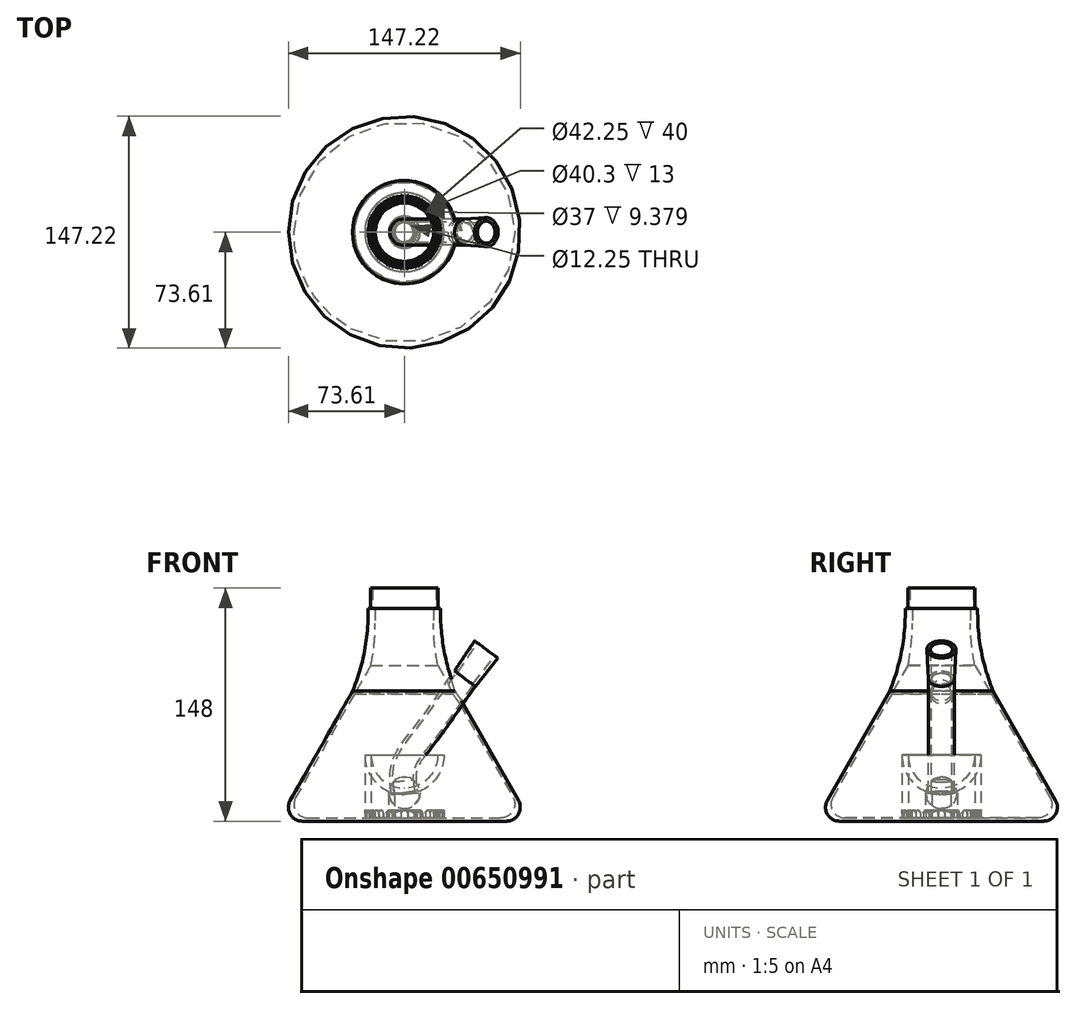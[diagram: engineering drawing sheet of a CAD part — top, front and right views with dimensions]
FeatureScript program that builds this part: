
annotation { "Feature Type Name" : "Feature", "Feature Type Description" : "" }
export const myFeature = defineFeature(function(context is Context, id is Id, definition is map)
    precondition{}
    {
        {
            var Q0;
            Q0=qCreatedBy(makeId("Front.planeOp"),FACE);
            var sketch = newSketch(context, id + "F0", { "sketchPlane" : qUnion([Q0])});
            skLineSegment(sketch, "E0", {"start": v(0, 0) * mm, "end": v(80, 0) * mm});
            skLineSegment(sketch, "E1", {"start": v(0, 0) * mm, "end": v(0, 100) * mm});
            skLineSegment(sketch, "E2", {"start": v(0, 100) * mm, "end": v(23, 100) * mm});
            skLineSegment(sketch, "E3", {"start": v(23, 100) * mm, "end": v(80, 0) * mm});
            skLineSegment(sketch, "E4.bottom", {"start": v(23, 100) * mm, "end": v(0, 100) * mm});
            skLineSegment(sketch, "E4.top", {"start": v(23, 135) * mm, "end": v(0, 135) * mm});
            skLineSegment(sketch, "E4.left", {"start": v(23, 100) * mm, "end": v(23, 135) * mm});
            skLineSegment(sketch, "E4.right", {"start": v(0, 100) * mm, "end": v(0, 135) * mm});
            skLineSegment(sketch, "E5.bottom", {"start": v(23, 100) * mm, "end": v(21.35, 100) * mm});
            skLineSegment(sketch, "E5.top", {"start": v(23, 135) * mm, "end": v(21.35, 135) * mm});
            skLineSegment(sketch, "E5.right", {"start": v(21.35, 100) * mm, "end": v(21.35, 135) * mm});
            skLineSegment(sketch, "E6.bottom", {"start": v(21.35, 100) * mm, "end": v(20.15, 100) * mm});
            skLineSegment(sketch, "E6.top", {"start": v(21.35, 135) * mm, "end": v(20.15, 135) * mm});
            skLineSegment(sketch, "E6.right", {"start": v(20.15, 100) * mm, "end": v(20.15, 135) * mm});
            skLineSegment(sketch, "E7", {"start": v(18.5, 135) * mm, "end": v(18.5, 100) * mm});
            skLineSegment(sketch, "E8.0", {"start": v(0.13, 2) * mm, "end": v(76.56, 2) * mm});
            skLineSegment(sketch, "E8.1", {"start": v(21.26, 99) * mm, "end": v(76.56, 2) * mm});
            skLineSegment(sketch, "E9", {"start": v(18.5, 100) * mm, "end": v(21.26, 99) * mm});
            skLineSegment(sketch, "E10.bottom", {"start": v(0.13, 2) * mm, "end": v(25.13, 2) * mm});
            skLineSegment(sketch, "E10.top", {"start": v(0.13, 42) * mm, "end": v(25.13, 42) * mm});
            skLineSegment(sketch, "E10.left", {"start": v(0.13, 2) * mm, "end": v(0.13, 42) * mm});
            skLineSegment(sketch, "E10.right", {"start": v(25.13, 2) * mm, "end": v(25.13, 42) * mm});
            skArc(sketch, "E11", {"start": v(25.13, 42) * mm, "mid": v(17.76, 59.72) * mm, "end": v(0, 67) * mm});
            skArc(sketch, "E12.0", {"start": v(21.13, 42) * mm, "mid": v(14.76, 57.06) * mm, "end": v(-0.49, 63) * mm});
            skLineSegment(sketch, "E12.1", {"start": v(21.13, 4.5) * mm, "end": v(21.13, 42) * mm});
            skLineSegment(sketch, "E13.bottom", {"start": v(0.13, 2) * mm, "end": v(2, 2) * mm});
            skLineSegment(sketch, "E13.top", {"start": v(0.13, 5) * mm, "end": v(2, 5) * mm});
            skLineSegment(sketch, "E13.left", {"start": v(0.13, 2) * mm, "end": v(0.13, 5) * mm});
            skLineSegment(sketch, "E13.right", {"start": v(2, 2) * mm, "end": v(2, 5) * mm});
            skArc(sketch, "E14", {"start": v(2, 5) * mm, "mid": v(1.4, 6.37) * mm, "end": v(0, 6.87) * mm});
            skLineSegment(sketch, "E15.MirrorCS", {"start": v(-2, 2) * mm, "end": v(-2, 5) * mm});
            skArc(sketch, "E16.MirrorCS", {"start": v(-2, 5) * mm, "mid": v(-1.4, 6.37) * mm, "end": v(0, 6.87) * mm});
            skLineSegment(sketch, "E17.MirrorCS", {"start": v(-0.13, 2) * mm, "end": v(-76.56, 2) * mm});
            skLineSegment(sketch, "E18.MirrorCS", {"start": v(23, 170) * mm, "end": v(23, 135) * mm});
            skLineSegment(sketch, "E19.MirrorCS", {"start": v(21.35, 170) * mm, "end": v(21.35, 135) * mm});
            skLineSegment(sketch, "E20.MirrorCS", {"start": v(20.15, 170) * mm, "end": v(20.15, 135) * mm});
            skLineSegment(sketch, "E21.MirrorCS", {"start": v(18.5, 135) * mm, "end": v(18.5, 170) * mm});
            skLineSegment(sketch, "E22.MirrorCS", {"start": v(0, 170) * mm, "end": v(0, 135) * mm});
            skLineSegment(sketch, "E23.MirrorCS", {"start": v(0, 170) * mm, "end": v(23, 170) * mm});
            skLineSegment(sketch, "E24.bottom", {"start": v(0.13, 2) * mm, "end": v(10.13, 2) * mm});
            skLineSegment(sketch, "E24.top", {"start": v(0.13, 18) * mm, "end": v(10.13, 18) * mm});
            skLineSegment(sketch, "E24.left", {"start": v(0.13, 2) * mm, "end": v(0.13, 18) * mm});
            skLineSegment(sketch, "E24.right", {"start": v(10.13, 2) * mm, "end": v(10.13, 18) * mm});
            skArc(sketch, "E25", {"start": v(10.13, 18) * mm, "mid": v(7.15, 25.12) * mm, "end": v(0, 28) * mm});
            skArc(sketch, "E26.0", {"start": v(6.13, 18) * mm, "mid": v(4.37, 22.24) * mm, "end": v(0.13, 24) * mm});
            skLineSegment(sketch, "E26.1", {"start": v(6.13, 4.5) * mm, "end": v(6.13, 18) * mm});
            skLineSegment(sketch, "E27", {"start": v(0, 28) * mm, "end": v(0.13, 42) * mm});
            skFitSpline(sketch, "E28", {"points": [v(0.13, 18) * mm, v(0.06, 35) * mm, v(14.76, 57.06) * mm, v(38.43, 90.52) * mm], "startDerivative": vector(-9.9, 64.12) * mm, "endDerivative": vector(59.19, 80.5) * mm});
            skLineSegment(sketch, "E29", {"start": v(0, 148) * mm, "end": v(23, 148) * mm});
            skLineSegment(sketch, "E30", {"start": v(38.43, 90.52) * mm, "end": v(3.42, 42) * mm});
            skLineSegment(sketch, "E31", {"start": v(3.42, 42) * mm, "end": v(56.06, 42) * mm});
            skLineSegment(sketch, "E32", {"start": v(8, 2) * mm, "end": v(41.32, 24.62) * mm});
            skLineSegment(sketch, "E33", {"start": v(6.13, 4.5) * mm, "end": v(6.13, 1.06) * mm});
            skLineSegment(sketch, "E34", {"start": v(6.13, 1.06) * mm, "end": v(21.13, 4.5) * mm});
            skLineSegment(sketch, "E35", {"start": v(21.13, 4.5) * mm, "end": v(21.13, 2) * mm});
            skLineSegment(sketch, "E36", {"start": v(0.13, 2) * mm, "end": v(-0.13, 2) * mm});
            skSolve(sketch);
        }
        {
            var Q0;
            {var subQ9=sQuery(id+"F0.wireOp",EDGE,"E0");Q0=makeQuery(id+"F0.imprint","IMPRINT",FACE,{"disambiguationData":[TD([[makeQuery(id+"F0.imprint","IMPRINT",EDGE,{"derivedFrom":subQ9}),1.0]])]});}
            var Q1;
            {var subQ0=sQuery(id+"F0.wireOp",EDGE,"E5.right");Q1=makeQuery(id+"F0.imprint","IMPRINT",FACE,{"disambiguationData":[TD([[makeQuery(id+"F0.imprint","IMPRINT",EDGE,{"derivedFrom":subQ0}),1.0]])]});}
            var Q2;
            {var subQ2=sQuery(id+"F0.wireOp",EDGE,"E4.left");Q2=makeQuery(id+"F0.imprint","IMPRINT",FACE,{"disambiguationData":[TD([[makeQuery(id+"F0.imprint","IMPRINT",EDGE,{"derivedFrom":subQ2}),1.0]])]});}
            var Q3;
            {var subQ0=sQuery(id+"F0.wireOp",EDGE,"E6.right");Q3=makeQuery(id+"F0.imprint","IMPRINT",FACE,{"disambiguationData":[TD([[makeQuery(id+"F0.imprint","IMPRINT",EDGE,{"derivedFrom":subQ0}),1.0]])]});}
            var Q4;
            {var subQ3=sQuery(id+"F0.wireOp",EDGE,"E19.MirrorCS");var subQ5=sQuery(id+"F0.wireOp",EDGE,"E29");var subQ6=makeQuery(id+"F0.imprint","INTERSECT",VERTEX,{"derivedFrom":[subQ3,subQ5]});Q4=makeQuery(id+"F0.imprint","IMPRINT",FACE,{"disambiguationData":[TD([[makeQuery(id+"F0.imprint","IMPRINT",EDGE,{"disambiguationData":[TD([[subQ6,1.0]])],"derivedFrom":subQ5}),-1.0]])]});}
            var Q5;
            {var subQ3=sQuery(id+"F0.wireOp",EDGE,"E9");Q5=makeQuery(id+"F0.imprint","IMPRINT",FACE,{"disambiguationData":[TD([[makeQuery(id+"F0.imprint","IMPRINT",EDGE,{"derivedFrom":subQ3}),1.0]])]});}
            var Q6;
            {var subQ0=sQuery(id+"F0.wireOp",EDGE,"E31");var subQ1=sQuery(id+"F0.wireOp",EDGE,"E3");var subQ2=makeQuery(id+"F0.imprint","INTERSECT",VERTEX,{"derivedFrom":[subQ1,subQ0]});Q6=makeQuery(id+"F0.imprint","IMPRINT",FACE,{"disambiguationData":[TD([[makeQuery(id+"F0.imprint","IMPRINT",EDGE,{"disambiguationData":[TD([[subQ2,1.0]])],"derivedFrom":subQ1}),-1.0]])]});}
            var Q7;
            {var subQ3=sQuery(id+"F0.wireOp",EDGE,"E8.0");var subQ7=makeQuery(id+"F0.imprint","INTERSECT",VERTEX,{"derivedFrom":[subQ3,sQuery(id+"F0.wireOp",EDGE,"E32")]});Q7=makeQuery(id+"F0.imprint","IMPRINT",FACE,{"disambiguationData":[TD([[makeQuery(id+"F0.imprint","IMPRINT",EDGE,{"disambiguationData":[TD([[subQ7,-1.0]])],"derivedFrom":subQ3}),-1.0]])]});}
            var Q8;
            Q8=sQuery(id+"F0.wireOp",EDGE,"E1");
            revolve(context, id + "F1", {"surfaceOperationType" : NewSurfaceOperationType.NEW, "entities" : qUnion([Q0, Q1, Q2, Q3, Q4, Q5, Q6, Q7]), "axis" : qUnion([Q8]), "revolveType" : RevolveType.FULL});
        }
        {
            var Q0;
            Q0=makeQuery(id+"F1.opRevolve","SWEPT_EDGE",EDGE,{"disambiguationData":[OSD([sQuery(id+"F0.wireOp",EDGE,"E0"),sQuery(id+"F0.wireOp",EDGE,"E3")])]});
            var Q1;
            Q1=makeQuery(id+"F1.opRevolve","SWEPT_EDGE",EDGE,{"disambiguationData":[OSD([sQuery(id+"F0.wireOp",EDGE,"E8.0"),sQuery(id+"F0.wireOp",EDGE,"E8.1")])]});
            fillet(context, id + "F2", {"entities" : qUnion([Q0, Q1]), "radius" : 8.87 * mm, "tangentPropagation" : true, "allowEdgeOverflow" : false});
        }
        {
            var Q0;
            Q0=makeQuery(id+"F1.opRevolve","SWEPT_EDGE",EDGE,{"disambiguationData":[OSD([sQuery(id+"F0.wireOp",EDGE,"E2"),sQuery(id+"F0.wireOp",EDGE,"E3"),sQuery(id+"F0.wireOp",EDGE,"E4.left")])]});
            var Q1;
            Q1=makeQuery(id+"F1.opRevolve","SWEPT_EDGE",EDGE,{"disambiguationData":[OSD([sQuery(id+"F0.wireOp",EDGE,"E2"),sQuery(id+"F0.wireOp",EDGE,"E7"),sQuery(id+"F0.wireOp",EDGE,"E9")])]});
            fillet(context, id + "F3", {"entities" : qUnion([Q0, Q1]), "radius" : 129.56 * mm, "tangentPropagation" : true, "allowEdgeOverflow" : false});
        }
        {
            var Q0;
            {var subQ4=sQuery(id+"F0.wireOp",EDGE,"E13.top");Q0=makeQuery(id+"F0.imprint","IMPRINT",FACE,{"disambiguationData":[TD([[makeQuery(id+"F0.imprint","IMPRINT",EDGE,{"derivedFrom":subQ4}),-1.0]])]});}
            var Q1;
            {var subQ3=sQuery(id+"F0.wireOp",EDGE,"E13.top");Q1=makeQuery(id+"F0.imprint","IMPRINT",FACE,{"disambiguationData":[TD([[makeQuery(id+"F0.imprint","IMPRINT",EDGE,{"derivedFrom":subQ3}),1.0]])]});}
            var Q2;
            {var subQ1=sQuery(id+"F0.wireOp",EDGE,"E15.MirrorCS");Q2=makeQuery(id+"F0.imprint","IMPRINT",FACE,{"disambiguationData":[TD([[makeQuery(id+"F0.imprint","IMPRINT",EDGE,{"derivedFrom":subQ1}),-1.0]])]});}
            var Q3;
            {var subQ0=sQuery(id+"F0.wireOp",EDGE,"E14");var subQ1=sQuery(id+"F0.wireOp",EDGE,"E10.left");var subQ2=makeQuery(id+"F0.imprint","INTERSECT",VERTEX,{"derivedFrom":[subQ1,subQ0]});Q3=makeQuery(id+"F0.imprint","IMPRINT",FACE,{"disambiguationData":[TD([[makeQuery(id+"F0.imprint","IMPRINT",EDGE,{"disambiguationData":[TD([[subQ2,1.0]])],"derivedFrom":subQ1}),1.0]])]});}
            extrude(context, id + "F4", {"entities" : qUnion([Q0, Q1, Q2, Q3]), "depth" : 30 * mm, "offsetDistance" : 25.4 * mm});
        }
        {
            var Q0;
            {var subQ0=sQuery(id+"F0.wireOp",EDGE,"E26.0");Q0=makeQuery(id+"F0.imprint","IMPRINT",FACE,{"disambiguationData":[TD([[makeQuery(id+"F0.imprint","IMPRINT",EDGE,{"derivedFrom":subQ0}),-1.0]])]});}
            var Q1;
            {var subQ0=sQuery(id+"F0.wireOp",EDGE,"E11");var subQ5=sQuery(id+"F0.wireOp",EDGE,"E28");var subQ6=makeQuery(id+"F0.imprint","INTERSECT",VERTEX,{"derivedFrom":[subQ0,subQ5]});var subQ8=makeQuery(id+"F0.imprint","IMPRINT",EDGE,{"disambiguationData":[TD([[subQ6,1.0]])],"derivedFrom":subQ5});var subQ13=sQuery(id+"F0.wireOp",EDGE,"E1");var subQ14=makeQuery(id+"F0.imprint","INTERSECT",VERTEX,{"derivedFrom":[subQ13,subQ0]});Q1=qUnion([makeQuery(id+"F0.imprint","IMPRINT",FACE,{"disambiguationData":[TD([[makeQuery(id+"F0.imprint","IMPRINT",EDGE,{"disambiguationData":[TD([[subQ14,1.0]])],"derivedFrom":subQ13}),-1.0]])]}),makeQuery(id+"F0.imprint","IMPRINT",FACE,{"disambiguationData":[TD([[makeQuery(id+"F0.imprint","IMPRINT",EDGE,{"disambiguationData":[TD([[subQ6,-1.0]])],"derivedFrom":subQ0}),1.0]])]}),makeQuery(id+"F0.imprint","IMPRINT",FACE,{"disambiguationData":[TD([[subQ8,-1.0]])]})]);}
            var Q2;
            {var subQ0=sQuery(id+"F0.wireOp",EDGE,"E10.right");var subQ5=sQuery(id+"F0.wireOp",EDGE,"E32");var subQ6=makeQuery(id+"F0.imprint","INTERSECT",VERTEX,{"derivedFrom":[subQ0,subQ5]});Q2=makeQuery(id+"F0.imprint","IMPRINT",FACE,{"disambiguationData":[TD([[makeQuery(id+"F0.imprint","IMPRINT",EDGE,{"disambiguationData":[TD([[subQ6,1.0]])],"derivedFrom":subQ5}),1.0]])]});}
            var Q3;
            {var subQ7=sQuery(id+"F0.wireOp",EDGE,"E35");Q3=makeQuery(id+"F0.imprint","IMPRINT",FACE,{"disambiguationData":[TD([[makeQuery(id+"F0.imprint","IMPRINT",EDGE,{"derivedFrom":subQ7}),1.0]])]});}
            var Q4;
            {var subQ3=sQuery(id+"F0.wireOp",EDGE,"E26.1");Q4=makeQuery(id+"F0.imprint","IMPRINT",FACE,{"disambiguationData":[TD([[makeQuery(id+"F0.imprint","IMPRINT",EDGE,{"derivedFrom":subQ3}),-1.0]])]});}
            var Q5;
            {var subQ0=sQuery(id+"F0.wireOp",EDGE,"E32");var subQ1=sQuery(id+"F0.wireOp",EDGE,"E8.0");var subQ2=makeQuery(id+"F0.imprint","INTERSECT",VERTEX,{"derivedFrom":[subQ1,subQ0]});Q5=makeQuery(id+"F0.imprint","IMPRINT",FACE,{"disambiguationData":[TD([[makeQuery(id+"F0.imprint","IMPRINT",EDGE,{"disambiguationData":[TD([[subQ2,-1.0]])],"derivedFrom":subQ1}),1.0]])]});}
            var Q6;
            Q6=sQuery(id+"F0.wireOp",EDGE,"E1");
            revolve(context, id + "F5", {"surfaceOperationType" : NewSurfaceOperationType.NEW, "entities" : qUnion([Q0, Q1, Q2, Q3, Q4, Q5]), "axis" : qUnion([Q6]), "revolveType" : RevolveType.FULL});
        }
        {
            var Q0;
            Q0=makeQuery(id+"F4.opExtrude","SWEPT_BODY",BODY,{"disambiguationData":[OSD([sQuery(id+"F0.wireOp",EDGE,"E8.0"),sQuery(id+"F0.wireOp",EDGE,"E13.right"),sQuery(id+"F0.wireOp",EDGE,"E14"),sQuery(id+"F0.wireOp",EDGE,"E15.MirrorCS"),sQuery(id+"F0.wireOp",EDGE,"E16.MirrorCS"),sQuery(id+"F0.wireOp",EDGE,"E17.MirrorCS"),sQuery(id+"F0.wireOp",EDGE,"E36")])]});
            var Q1;
            Q1=sQuery(id+"F0.wireOp",EDGE,"E24.left");
            circularPattern(context, id + "F6", {"operationType" : NewBodyOperationType.REMOVE, "entities" : qUnion([Q0]), "axis" : qUnion([Q1]), "angle" : 360 * degree, "instanceCount" : 16, "equalSpace" : true});
        }
        {
            var Q0;
            {var subQ4=sQuery(id+"F0.wireOp",EDGE,"E13.top");Q0=makeQuery(id+"F0.imprint","IMPRINT",FACE,{"disambiguationData":[TD([[makeQuery(id+"F0.imprint","IMPRINT",EDGE,{"derivedFrom":subQ4}),-1.0]])]});}
            var Q1;
            {var subQ3=sQuery(id+"F0.wireOp",EDGE,"E13.top");Q1=makeQuery(id+"F0.imprint","IMPRINT",FACE,{"disambiguationData":[TD([[makeQuery(id+"F0.imprint","IMPRINT",EDGE,{"derivedFrom":subQ3}),1.0]])]});}
            var Q2;
            {var subQ1=sQuery(id+"F0.wireOp",EDGE,"E15.MirrorCS");Q2=makeQuery(id+"F0.imprint","IMPRINT",FACE,{"disambiguationData":[TD([[makeQuery(id+"F0.imprint","IMPRINT",EDGE,{"derivedFrom":subQ1}),-1.0]])]});}
            var Q3;
            {var subQ0=sQuery(id+"F0.wireOp",EDGE,"E14");var subQ1=sQuery(id+"F0.wireOp",EDGE,"E10.left");var subQ2=makeQuery(id+"F0.imprint","INTERSECT",VERTEX,{"derivedFrom":[subQ1,subQ0]});Q3=makeQuery(id+"F0.imprint","IMPRINT",FACE,{"disambiguationData":[TD([[makeQuery(id+"F0.imprint","IMPRINT",EDGE,{"disambiguationData":[TD([[subQ2,1.0]])],"derivedFrom":subQ1}),1.0]])]});}
            extrude(context, id + "F7", {"entities" : qUnion([Q0, Q1, Q2, Q3]), "depth" : 25.4 * mm, "offsetDistance" : 25.4 * mm});
        }
        {
            var Q0;
            Q0=makeQuery(id+"F7.opExtrude","SWEPT_BODY",BODY,{"disambiguationData":[OSD([sQuery(id+"F0.wireOp",EDGE,"E8.0"),sQuery(id+"F0.wireOp",EDGE,"E13.right"),sQuery(id+"F0.wireOp",EDGE,"E14"),sQuery(id+"F0.wireOp",EDGE,"E15.MirrorCS"),sQuery(id+"F0.wireOp",EDGE,"E16.MirrorCS"),sQuery(id+"F0.wireOp",EDGE,"E17.MirrorCS"),sQuery(id+"F0.wireOp",EDGE,"E36")])]});
            var Q1;
            Q1=makeQuery(id+"F5.opRevolve","SWEPT_FACE",FACE,{"disambiguationData":[OSD([sQuery(id+"F0.wireOp",EDGE,"E10.right")])]});
            circularPattern(context, id + "F8", {"operationType" : NewBodyOperationType.REMOVE, "entities" : qUnion([Q0]), "axis" : qUnion([Q1]), "angle" : 360 * degree, "instanceCount" : 8, "equalSpace" : true});
        }
        {
            var Q0;
            Q0=sQuery(id+"F0.wireOp",VERTEX,"E28.3.internal");
            var Q1;
            Q1=sQuery(id+"F0.wireOp",EDGE,"E28");
            cPlane(context, id + "F9", {"entities" : qUnion([Q0, Q1]), "cplaneType" : CPlaneType.CURVE_POINT, "offset" : 25.4 * mm, "width" : 152.4 * mm, "height" : 152.4 * mm});
        }
        {
            var Q0;
            Q0=qCreatedBy(id+"F9.planeOp",FACE);
            var sketch = newSketch(context, id + "F10", { "sketchPlane" : qUnion([Q0])});
            skPoint(sketch, "E37.0", {"position": v(-22.66, 0) * mm});
            skCircle(sketch, "E38", {"center": v(-22.66, 0) * mm, "radius": 6.5 * mm});
            skCircle(sketch, "E39", {"center": v(-22.66, 0) * mm, "radius": 8.25 * mm});
            skSolve(sketch);
        }
        {
            var Q0;
            Q0=makeQuery(id+"F10.imprint","IMPRINT",FACE,{"disambiguationData":[TD([[makeQuery(id+"F10.imprint","IMPRINT",EDGE,{"derivedFrom":sQuery(id+"F10.wireOp",EDGE,"E38")}),1.0]])]});
            var Q1;
            Q1=makeQuery(id+"F10.imprint","IMPRINT",FACE,{"disambiguationData":[TD([[makeQuery(id+"F10.imprint","IMPRINT",EDGE,{"derivedFrom":sQuery(id+"F10.wireOp",EDGE,"E38")}),-1.0]])]});
            var Q2;
            Q2=sQuery(id+"F0.wireOp",EDGE,"E28");
            sweep(context, id + "F11", {"profiles" : qUnion([Q0, Q1]), "path" : qUnion([Q2])});
        }
        {
            var Q0;
            Q0=makeQuery(id+"F10.imprint","IMPRINT",FACE,{"disambiguationData":[TD([[makeQuery(id+"F10.imprint","IMPRINT",EDGE,{"derivedFrom":sQuery(id+"F10.wireOp",EDGE,"E38")}),1.0]])]});
            var Q1;
            Q1=sQuery(id+"F0.wireOp",EDGE,"E28");
            sweep(context, id + "F12", {"operationType" : NewBodyOperationType.REMOVE, "profiles" : qUnion([Q0]), "path" : qUnion([Q1])});
        }
        {
            var Q0;
            {var subQ3=sQuery(id+"F0.wireOp",EDGE,"E13.right");Q0=makeQuery(id+"F0.imprint","IMPRINT",FACE,{"disambiguationData":[TD([[makeQuery(id+"F0.imprint","IMPRINT",EDGE,{"derivedFrom":subQ3}),-1.0]])]});}
            var Q1;
            {var subQ3=sQuery(id+"F0.wireOp",EDGE,"E26.0");Q1=makeQuery(id+"F0.imprint","IMPRINT",FACE,{"disambiguationData":[TD([[makeQuery(id+"F0.imprint","IMPRINT",EDGE,{"derivedFrom":subQ3}),1.0]])]});}
            var Q2;
            Q2=sQuery(id+"F0.wireOp",EDGE,"E1");
            revolve(context, id + "F13", {"operationType" : NewBodyOperationType.REMOVE, "entities" : qUnion([Q0, Q1]), "axis" : qUnion([Q2]), "revolveType" : RevolveType.FULL, "oppositeDirection" : true});
        }
        {
            var Q0;
            Q0=qCreatedBy(makeId("Front.planeOp"),FACE);
            var sketch = newSketch(context, id + "F14", { "sketchPlane" : qUnion([Q0])});
            skLineSegment(sketch, "E40.0", {"start": v(45.08, 85.63) * mm, "end": v(31.79, 95.4) * mm});
            skPoint(sketch, "E41.0", {"position": v(38.43, 90.52) * mm});
            skLineSegment(sketch, "E42", {"start": v(38.43, 90.52) * mm, "end": v(52.06, 109.05) * mm});
            skLineSegment(sketch, "E43.0", {"start": v(43.67, 86.67) * mm, "end": v(33.2, 94.37) * mm});
            skLineSegment(sketch, "E44", {"start": v(38.43, 90.52) * mm, "end": v(43.27, 86.96) * mm});
            skLineSegment(sketch, "E45", {"start": v(52.06, 109.05) * mm, "end": v(57.7, 104.9) * mm});
            skLineSegment(sketch, "E46", {"start": v(57.7, 104.9) * mm, "end": v(43.27, 86.96) * mm});
            skLineSegment(sketch, "E47", {"start": v(45.08, 85.63) * mm, "end": v(59.51, 103.57) * mm});
            skLineSegment(sketch, "E48", {"start": v(57.7, 104.9) * mm, "end": v(59.51, 103.57) * mm});
            skSolve(sketch);
        }
        {
            var Q0;
            {var subQ4=sQuery(id+"F14.wireOp",EDGE,"E46");Q0=makeQuery(id+"F14.imprint","IMPRINT",FACE,{"disambiguationData":[TD([[makeQuery(id+"F14.imprint","IMPRINT",EDGE,{"derivedFrom":subQ4}),1.0]])]});}
            var Q1;
            Q1=sQuery(id+"F14.wireOp",EDGE,"E42");
            revolve(context, id + "F15", {"operationType" : NewBodyOperationType.ADD, "entities" : qUnion([Q0]), "axis" : qUnion([Q1]), "revolveType" : RevolveType.FULL, "surfaceOperationType" : NewSurfaceOperationType.NEW});
        }
    });
